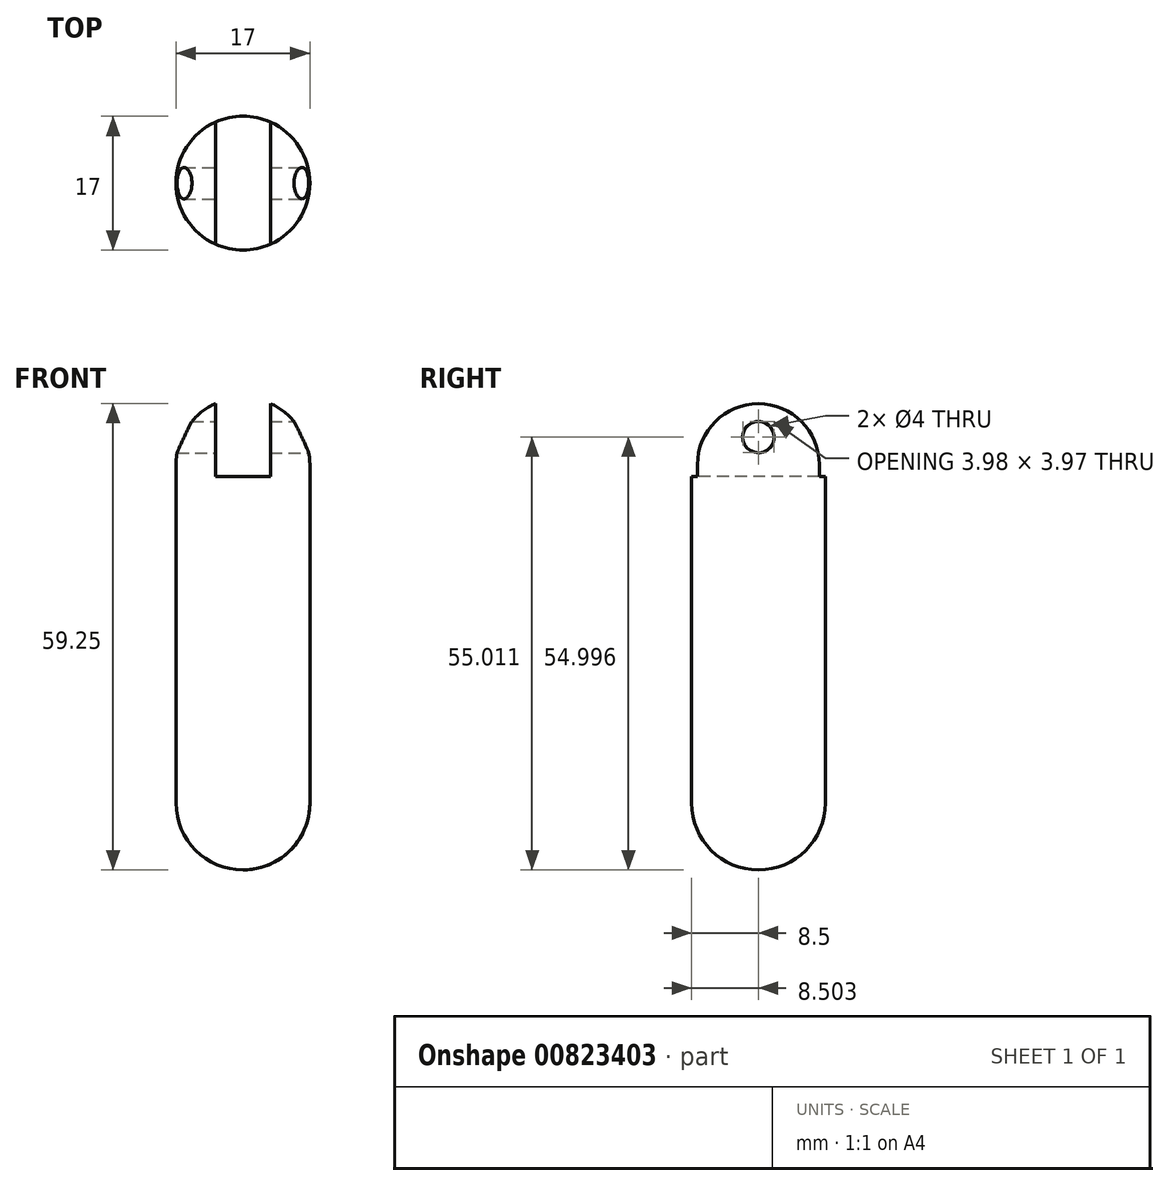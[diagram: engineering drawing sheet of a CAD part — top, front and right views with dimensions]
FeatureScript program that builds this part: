
annotation { "Feature Type Name" : "Feature", "Feature Type Description" : "" }
export const myFeature = defineFeature(function(context is Context, id is Id, definition is map)
    precondition{}
    {
        {
            var Q0;
            Q0=qCreatedBy(makeId("Top.planeOp"),FACE);
            var sketch = newSketch(context, id + "F0", { "sketchPlane" : qUnion([Q0])});
            skCircle(sketch, "E0", {"center": v(0, 0) * mm, "radius": 8.5 * mm});
            skSolve(sketch);
        }
        {
            var Q0;
            Q0 = qSketchRegion(id + "F0", true);
            extrude(context, id + "F1", {"entities" : qUnion([Q0]), "endBound" : BoundingType.SYMMETRIC, "depth" : 60 * mm, "offsetDistance" : 25 * mm});
        }
        {
            var Q0;
            Q0=makeQuery(id+"F1.opExtrude","CAP_EDGE",EDGE,{"disambiguationData":[OSD([sQuery(id+"F0.wireOp",EDGE,"E0")])],"isStart":false});
            fillet(context, id + "F2", {"entities" : qUnion([Q0]), "radius" : 8.5 * mm, "tangentPropagation" : true, "allowEdgeOverflow" : false});
        }
        {
            var Q0;
            Q0=makeQuery(id+"F1.opExtrude","CAP_EDGE",EDGE,{"disambiguationData":[OSD([sQuery(id+"F0.wireOp",EDGE,"E0")])],"isStart":true});
            fillet(context, id + "F3", {"entities" : qUnion([Q0]), "radius" : 8.5 * mm, "tangentPropagation" : true, "allowEdgeOverflow" : false});
        }
        {
            var Q0;
            Q0=qCreatedBy(makeId("Top.planeOp"),FACE);
            cPlane(context, id + "F4", {"entities" : qUnion([Q0]), "cplaneType" : CPlaneType.OFFSET, "offset" : 30 * mm, "width" : 150 * mm, "height" : 150 * mm});
        }
        {
            var Q0;
            Q0=qCreatedBy(id+"F4.planeOp",FACE);
            var sketch = newSketch(context, id + "F5", { "sketchPlane" : qUnion([Q0])});
            skLineSegment(sketch, "E1.bottom", {"start": v(3.5, 12.42) * mm, "end": v(-3.5, 12.42) * mm});
            skLineSegment(sketch, "E1.top", {"start": v(3.5, -12.42) * mm, "end": v(-3.5, -12.42) * mm});
            skLineSegment(sketch, "E1.left", {"start": v(3.5, 12.42) * mm, "end": v(3.5, -12.42) * mm});
            skLineSegment(sketch, "E1.right", {"start": v(-3.5, 12.42) * mm, "end": v(-3.5, -12.42) * mm});
            skPoint(sketch, "E1.middle", {"position": v(0, 0) * mm});
            skSolve(sketch);
        }
        {
            var Q0;
            Q0 = qSketchRegion(id + "F5", true);
            extrude(context, id + "F6", {"entities" : qUnion([Q0]), "operationType" : NewBodyOperationType.REMOVE, "oppositeDirection" : true, "depth" : 10 * mm, "offsetDistance" : 25 * mm});
        }
        {
            var Q0;
            Q0=qCreatedBy(makeId("Right.planeOp"),FACE);
            var sketch = newSketch(context, id + "F7", { "sketchPlane" : qUnion([Q0])});
            skCircle(sketch, "E2", {"center": v(0, 25) * mm, "radius": 2 * mm});
            skSolve(sketch);
        }
        {
            var Q0;
            Q0 = qSketchRegion(id + "F7", true);
            extrude(context, id + "F8", {"entities" : qUnion([Q0]), "operationType" : NewBodyOperationType.REMOVE, "endBound" : BoundingType.SYMMETRIC, "oppositeDirection" : true, "depth" : 25 * mm, "offsetDistance" : 25 * mm});
        }
    });
